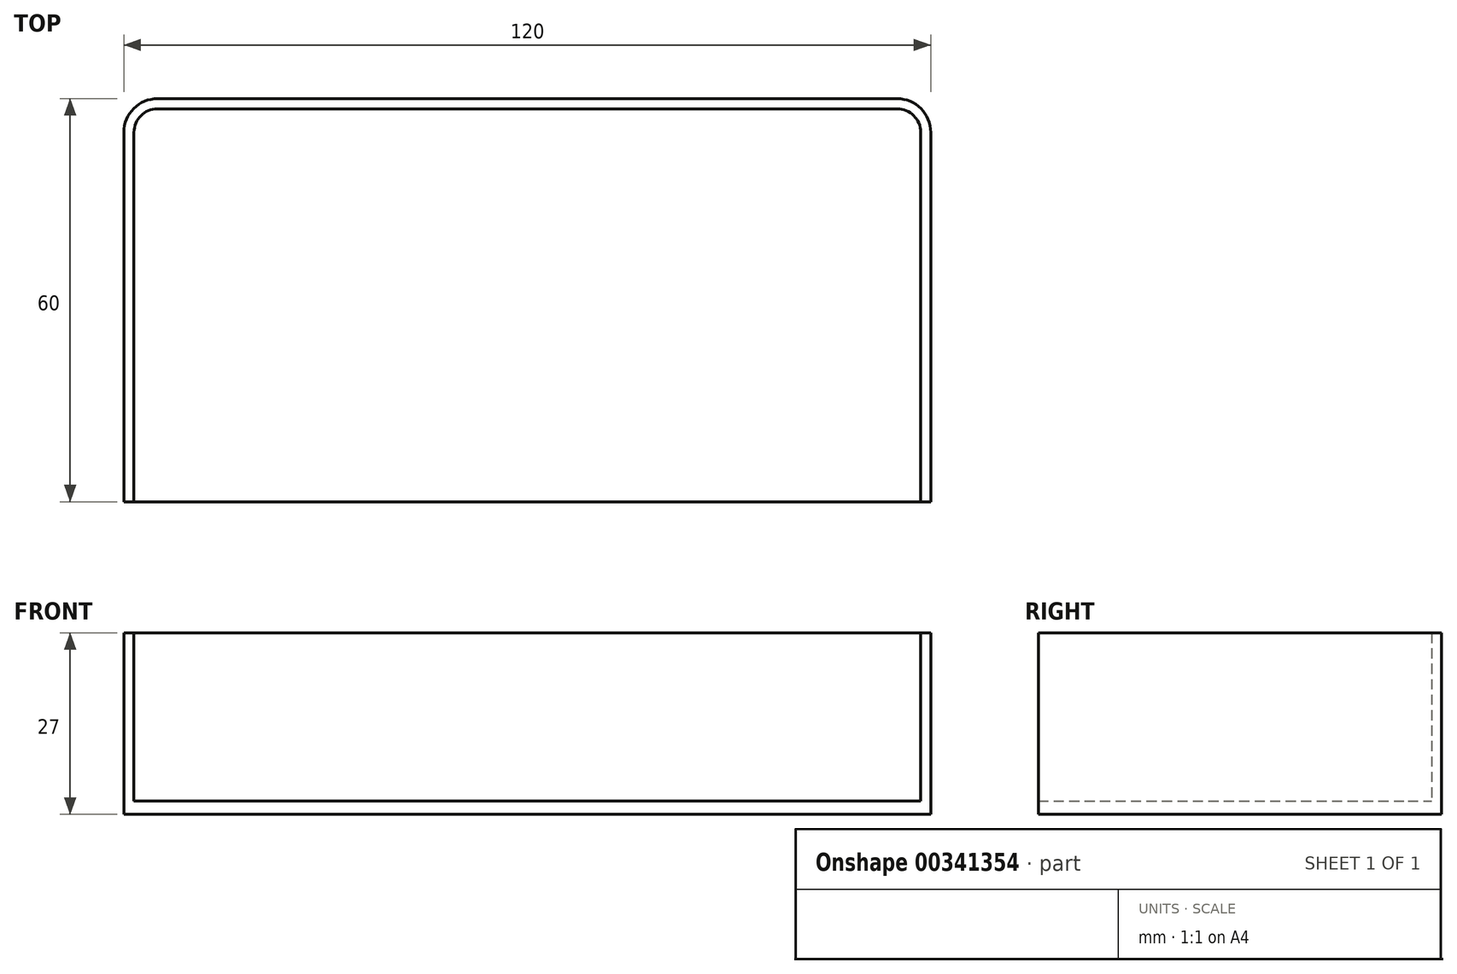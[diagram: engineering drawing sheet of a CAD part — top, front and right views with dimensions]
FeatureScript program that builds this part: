
annotation { "Feature Type Name" : "Feature", "Feature Type Description" : "" }
export const myFeature = defineFeature(function(context is Context, id is Id, definition is map)
    precondition{}
    {
        {
            var Q0;
            Q0=qCreatedBy(makeId("Top.planeOp"),FACE);
            var sketch = newSketch(context, id + "F0", { "sketchPlane" : qUnion([Q0])});
            skLineSegment(sketch, "E0.bottom", {"start": v(0, 0) * mm, "end": v(120, 0) * mm});
            skLineSegment(sketch, "E0.top", {"start": v(5, 60) * mm, "end": v(115, 60) * mm});
            skLineSegment(sketch, "E0.left", {"start": v(0, 0) * mm, "end": v(0, 55) * mm});
            skLineSegment(sketch, "E0.right", {"start": v(120, 0) * mm, "end": v(120, 55) * mm});
            skPoint(sketch, "E1.visualSharp", {"position": v(0, 60) * mm});
            skArc(sketch, "E1.filletArc", {"start": v(5, 60) * mm, "mid": v(1.46, 58.54) * mm, "end": v(0, 55) * mm});
            skPoint(sketch, "E2.visualSharp", {"position": v(120, 60) * mm});
            skArc(sketch, "E2.filletArc", {"start": v(120, 55) * mm, "mid": v(118.54, 58.54) * mm, "end": v(115, 60) * mm});
            skSolve(sketch);
        }
        {
            var Q0;
            Q0 = qSketchRegion(id + "F0", true);
            extrude(context, id + "F1", {"entities" : qUnion([Q0]), "depth" : 2 * mm});
        }
        {
            var Q0;
            Q0=makeQuery(id+"F1.opExtrude","CAP_FACE",FACE,{"disambiguationData":[OSD([sQuery(id+"F0.wireOp",EDGE,"E0.bottom"),sQuery(id+"F0.wireOp",EDGE,"E0.top"),sQuery(id+"F0.wireOp",EDGE,"E0.left"),sQuery(id+"F0.wireOp",EDGE,"E0.right"),sQuery(id+"F0.wireOp",EDGE,"E1.filletArc"),sQuery(id+"F0.wireOp",EDGE,"E2.filletArc")])],"isStart":false});
            var sketch = newSketch(context, id + "F2", { "sketchPlane" : qUnion([Q0])});
            skLineSegment(sketch, "E3.0", {"start": v(0, 0) * mm, "end": v(0, 55) * mm});
            skArc(sketch, "E4.0", {"start": v(5, 60) * mm, "mid": v(1.46, 58.54) * mm, "end": v(0, 55) * mm});
            skLineSegment(sketch, "E5.0", {"start": v(5, 60) * mm, "end": v(115, 60) * mm});
            skArc(sketch, "E6.0", {"start": v(120, 55) * mm, "mid": v(118.54, 58.54) * mm, "end": v(115, 60) * mm});
            skLineSegment(sketch, "E7.0", {"start": v(120, 0) * mm, "end": v(120, 55) * mm});
            skLineSegment(sketch, "E8.0", {"start": v(118.5, 0) * mm, "end": v(118.5, 55) * mm});
            skLineSegment(sketch, "E8.1", {"start": v(1.5, 0) * mm, "end": v(1.5, 55) * mm});
            skArc(sketch, "E8.2", {"start": v(5, 58.5) * mm, "mid": v(2.53, 57.47) * mm, "end": v(1.5, 55) * mm});
            skLineSegment(sketch, "E8.3", {"start": v(5, 58.5) * mm, "end": v(115, 58.5) * mm});
            skArc(sketch, "E8.4", {"start": v(118.5, 55) * mm, "mid": v(117.47, 57.47) * mm, "end": v(115, 58.5) * mm});
            skLineSegment(sketch, "E9", {"start": v(1.5, 0) * mm, "end": v(0, 0) * mm});
            skLineSegment(sketch, "E10", {"start": v(118.5, 0) * mm, "end": v(120, 0) * mm});
            skSolve(sketch);
        }
        {
            var Q0;
            Q0 = qSketchRegion(id + "F2", true);
            extrude(context, id + "F3", {"entities" : qUnion([Q0]), "operationType" : NewBodyOperationType.ADD, "depth" : 25 * mm});
        }
    });
